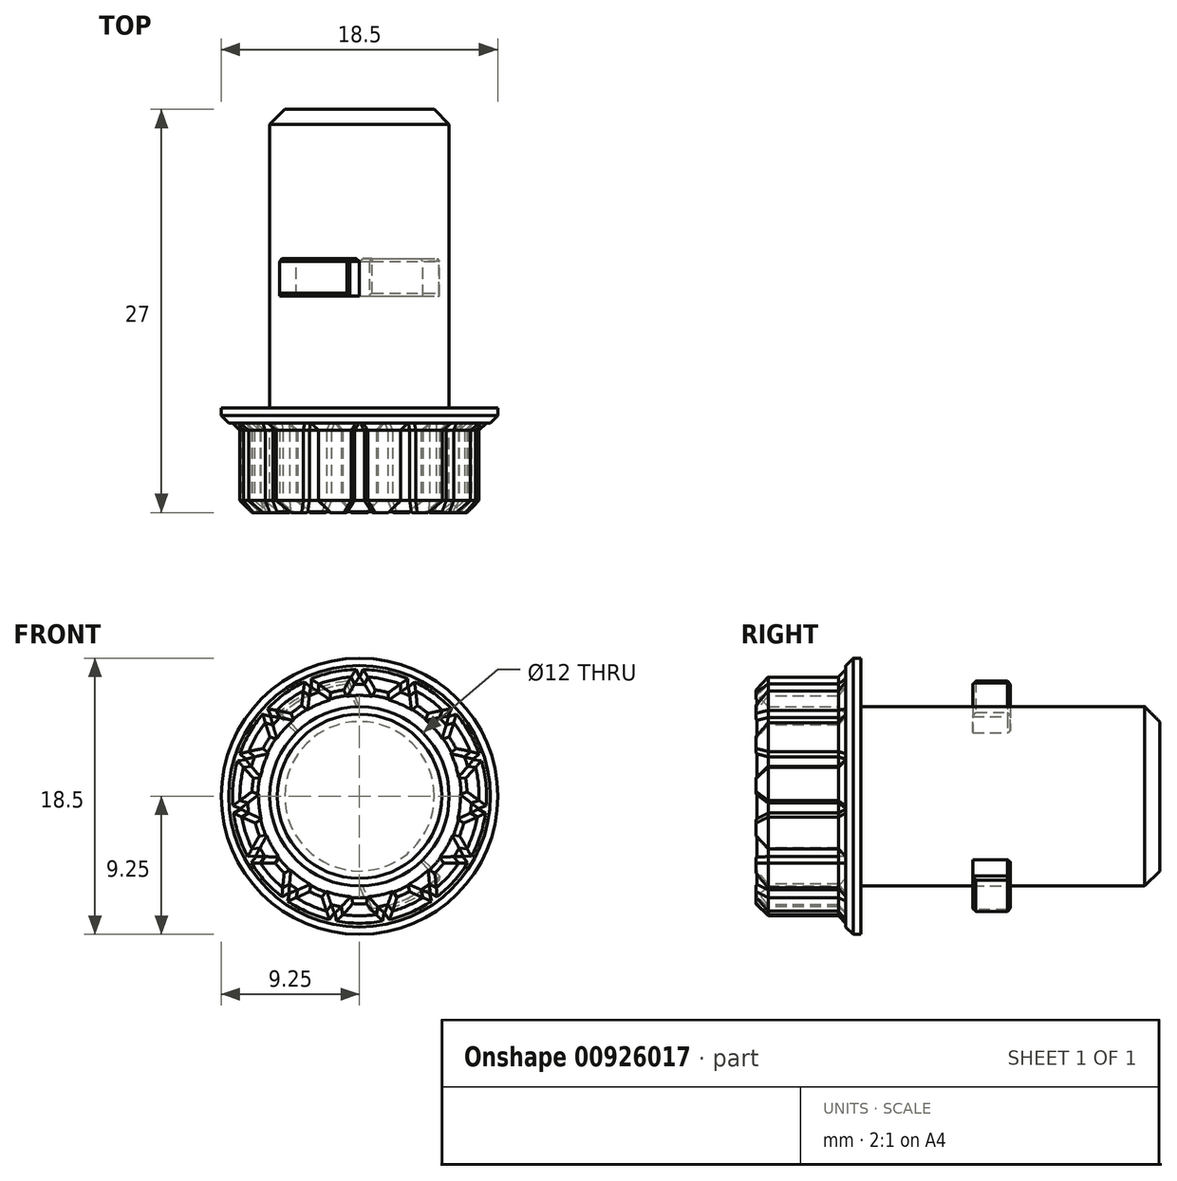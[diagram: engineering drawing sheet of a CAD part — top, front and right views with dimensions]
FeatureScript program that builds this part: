
annotation { "Feature Type Name" : "Feature", "Feature Type Description" : "" }
export const myFeature = defineFeature(function(context is Context, id is Id, definition is map)
    precondition{}
    {
        {
            var Q0;
            Q0=qCreatedBy(makeId("Front.planeOp"),FACE);
            var sketch = newSketch(context, id + "F0", { "sketchPlane" : qUnion([Q0])});
            skCircle(sketch, "E0", {"center": v(0, 0) * mm, "radius": 6 * mm});
            skArc(sketch, "E1", {"start": v(0.7, -7.72) * mm, "mid": v(3.29, -7.02) * mm, "end": v(5.48, -5.48) * mm});
            skLineSegment(sketch, "E2", {"start": v(-4.24, 4.24) * mm, "end": v(-5.48, 5.48) * mm});
            skLineSegment(sketch, "E3", {"start": v(4.24, -4.24) * mm, "end": v(5.48, -5.48) * mm});
            skArc(sketch, "E4.trimOffspring", {"start": v(-0.7, 7.72) * mm, "mid": v(-3.29, 7.02) * mm, "end": v(-5.48, 5.48) * mm});
            skLineSegment(sketch, "E5", {"start": v(0, 6) * mm, "end": v(-0.7, 7.72) * mm});
            skLineSegment(sketch, "E6", {"start": v(0, -6) * mm, "end": v(0.7, -7.72) * mm});
            skPoint(sketch, "E7.orphan", {"position": v(0, 7.75) * mm});
            skSolve(sketch);
        }
        {
            var Q0;
            Q0=qSketchRegion(id+"F0",true);
            extrude(context, id + "F1", {"entities" : qUnion([Q0]), "depth" : 10 * mm, "offsetDistance" : 25 * mm});
        }
        {
            var Q0;
            Q0=makeQuery(id+"F1.opExtrude","CAP_FACE",FACE,{"disambiguationData":[OSD([sQuery(id+"F0.wireOp",EDGE,"E0"),sQuery(id+"F0.wireOp",EDGE,"E1"),sQuery(id+"F0.wireOp",EDGE,"E2"),sQuery(id+"F0.wireOp",EDGE,"E3"),sQuery(id+"F0.wireOp",EDGE,"E4.trimOffspring"),sQuery(id+"F0.wireOp",EDGE,"E5"),sQuery(id+"F0.wireOp",EDGE,"E6")])],"isStart":false});
            var sketch = newSketch(context, id + "F2", { "sketchPlane" : qUnion([Q0])});
            skCircle(sketch, "E8", {"center": v(0, 0) * mm, "radius": 6 * mm});
            skSolve(sketch);
        }
        {
            var Q0;
            {var subQ1=makeQuery(id+"F1.opExtrude","CAP_EDGE",EDGE,{"disambiguationData":[OSD([sQuery(id+"F0.wireOp",EDGE,"E2")])],"isStart":false});Q0=makeQuery(id+"F2.imprint","IMPRINT",FACE,{"disambiguationData":[TD([[makeQuery(id+"F2.imprint","IMPRINT",EDGE,{"derivedFrom":subQ1}),-1.0]])]});}
            var Q1;
            Q1=makeQuery(id+"F2.imprint","IMPRINT",FACE,{"disambiguationData":[TD([[makeQuery(id+"F2.imprint","IMPRINT",EDGE,{"derivedFrom":makeQuery(id+"F1.opExtrude","CAP_EDGE",EDGE,{"disambiguationData":[OSD([sQuery(id+"F0.wireOp",EDGE,"E1")])],"isStart":false})}),1.0]])]});
            extrude(context, id + "F3", {"entities" : qUnion([Q0, Q1]), "operationType" : NewBodyOperationType.REMOVE, "oppositeDirection" : true, "depth" : 7.5 * mm, "offsetDistance" : 25 * mm});
        }
        {
            var Q0;
            Q0=makeQuery(id+"F1.opExtrude","CAP_FACE",FACE,{"disambiguationData":[OSD([sQuery(id+"F0.wireOp",EDGE,"E0"),sQuery(id+"F0.wireOp",EDGE,"E1"),sQuery(id+"F0.wireOp",EDGE,"E2"),sQuery(id+"F0.wireOp",EDGE,"E3"),sQuery(id+"F0.wireOp",EDGE,"E4.trimOffspring"),sQuery(id+"F0.wireOp",EDGE,"E5"),sQuery(id+"F0.wireOp",EDGE,"E6")])],"isStart":false});
            var sketch = newSketch(context, id + "F4", { "sketchPlane" : qUnion([Q0])});
            skCircle(sketch, "E9", {"center": v(0, 0) * mm, "radius": 8 * mm});
            skSolve(sketch);
        }
        {
            var Q0;
            Q0=makeQuery(id+"F4.imprint","IMPRINT",FACE,{"disambiguationData":[TD([[makeQuery(id+"F4.imprint","IMPRINT",EDGE,{"derivedFrom":sQuery(id+"F4.wireOp",EDGE,"E9")}),1.0]])]});
            var Q1;
            {var subQ0=sQuery(id+"F2.wireOp",EDGE,"E8");var subQ1=sQuery(id+"F0.wireOp",EDGE,"E3");var subQ3=sQuery(id+"F0.wireOp",EDGE,"E2");var subQ5=sQuery(id+"F0.wireOp",EDGE,"E0");Q1=makeQuery(id+"F4.imprint","IMPRINT",FACE,{"disambiguationData":[TD([[makeQuery(id+"F4.imprint","IMPRINT",EDGE,{"derivedFrom":makeQuery(id+"F3.boolean.opBoolean","MERGE",EDGE,{"derivedFrom":[makeQuery(id+"F1.opExtrude","CAP_EDGE",EDGE,{"disambiguationData":[OSD([subQ5]),TDD([makeQuery(id+"F0.imprint","IMPRINT",EDGE,{"disambiguationData":[TD([[makeQuery(id+"F0.imprint","INTERSECT",VERTEX,{"derivedFrom":[subQ5,subQ3]}),-1.0]])],"derivedFrom":subQ5})])],"isStart":false}),makeQuery(id+"F1.opExtrude","CAP_EDGE",EDGE,{"disambiguationData":[OSD([subQ5]),TDD([makeQuery(id+"F0.imprint","IMPRINT",EDGE,{"disambiguationData":[TD([[makeQuery(id+"F0.imprint","INTERSECT",VERTEX,{"derivedFrom":[subQ5,subQ1]}),-1.0]])],"derivedFrom":subQ5})])],"isStart":false})],"fromTools":[makeQuery(id+"F3.opExtrude","CAP_EDGE",EDGE,{"disambiguationData":[OSD([subQ0]),TDD([makeQuery(id+"F2.imprint","IMPRINT",EDGE,{"disambiguationData":[TD([[makeQuery(id+"F2.imprint","INTERSECT",VERTEX,{"derivedFrom":[makeQuery(id+"F1.opExtrude","CAP_EDGE",EDGE,{"disambiguationData":[OSD([subQ3])],"isStart":false}),subQ0]}),1.0]])],"derivedFrom":subQ0})])],"isStart":true}),makeQuery(id+"F3.opExtrude","CAP_EDGE",EDGE,{"disambiguationData":[OSD([subQ0]),TDD([makeQuery(id+"F2.imprint","IMPRINT",EDGE,{"disambiguationData":[TD([[makeQuery(id+"F2.imprint","INTERSECT",VERTEX,{"derivedFrom":[makeQuery(id+"F1.opExtrude","CAP_EDGE",EDGE,{"disambiguationData":[OSD([subQ1])],"isStart":false}),subQ0]}),1.0]])],"derivedFrom":subQ0})])],"isStart":true})]})}),1.0]])]});}
            extrude(context, id + "F5", {"entities" : qUnion([Q0, Q1]), "operationType" : NewBodyOperationType.ADD, "depth" : 7 * mm, "offsetDistance" : 25 * mm});
        }
        {
            var Q0;
            Q0=makeQuery(id+"F1.opExtrude","CAP_FACE",FACE,{"disambiguationData":[OSD([sQuery(id+"F0.wireOp",EDGE,"E0"),sQuery(id+"F0.wireOp",EDGE,"E1"),sQuery(id+"F0.wireOp",EDGE,"E2"),sQuery(id+"F0.wireOp",EDGE,"E3"),sQuery(id+"F0.wireOp",EDGE,"E4.trimOffspring"),sQuery(id+"F0.wireOp",EDGE,"E5"),sQuery(id+"F0.wireOp",EDGE,"E6")])],"isStart":true});
            var sketch = newSketch(context, id + "F6", { "sketchPlane" : qUnion([Q0])});
            skCircle(sketch, "E10", {"center": v(0, 0) * mm, "radius": 6 * mm});
            skSolve(sketch);
        }
        {
            var Q0;
            Q0=qSketchRegion(id+"F6",true);
            extrude(context, id + "F7", {"entities" : qUnion([Q0]), "operationType" : NewBodyOperationType.ADD, "depth" : 10 * mm, "offsetDistance" : 25 * mm});
        }
        {
            var Q0;
            Q0=makeQuery(id+"F5.opExtrude","CAP_FACE",FACE,{"disambiguationData":[OSD([sQuery(id+"F4.wireOp",EDGE,"E9")])],"isStart":false});
            var sketch = newSketch(context, id + "F8", { "sketchPlane" : qUnion([Q0])});
            skCircle(sketch, "E11", {"center": v(0, 0) * mm, "radius": 7.5 * mm});
            skLineSegment(sketch, "E12", {"start": v(-0.56, 7.98) * mm, "end": v(-0.34, 7.5) * mm});
            skLineSegment(sketch, "E13", {"start": v(0.56, 7.98) * mm, "end": v(0.34, 7.5) * mm});
            skLineSegment(sketch, "E14.1.0", {"start": v(-2.74, 7.52) * mm, "end": v(-2.74, 6.98) * mm});
            skLineSegment(sketch, "E14.1.1", {"start": v(-3.76, 7.06) * mm, "end": v(-3.36, 6.7) * mm});
            skLineSegment(sketch, "E14.2.0", {"start": v(-5.56, 5.75) * mm, "end": v(-5.34, 5.27) * mm});
            skLineSegment(sketch, "E14.2.1", {"start": v(-6.3, 4.93) * mm, "end": v(-5.8, 4.76) * mm});
            skLineSegment(sketch, "E14.3.0", {"start": v(-7.42, 3) * mm, "end": v(-7.02, 2.64) * mm});
            skLineSegment(sketch, "E14.3.1", {"start": v(-7.76, 1.94) * mm, "end": v(-7.23, 2) * mm});
            skLineSegment(sketch, "E14.4.0", {"start": v(-8, -0.28) * mm, "end": v(-7.49, -0.44) * mm});
            skLineSegment(sketch, "E14.4.1", {"start": v(-7.88, -1.39) * mm, "end": v(-7.42, -1.12) * mm});
            skLineSegment(sketch, "E14.5.0", {"start": v(-7.2, -3.5) * mm, "end": v(-6.66, -3.45) * mm});
            skLineSegment(sketch, "E14.5.1", {"start": v(-6.63, -4.47) * mm, "end": v(-6.32, -4.04) * mm});
            skLineSegment(sketch, "E14.6.0", {"start": v(-5.14, -6.13) * mm, "end": v(-4.68, -5.86) * mm});
            skLineSegment(sketch, "E14.6.1", {"start": v(-4.24, -6.78) * mm, "end": v(-4.13, -6.26) * mm});
            skLineSegment(sketch, "E14.7.0", {"start": v(-2.2, -7.7) * mm, "end": v(-1.9, -7.26) * mm});
            skLineSegment(sketch, "E14.7.1", {"start": v(-1.11, -7.92) * mm, "end": v(-1.22, -7.4) * mm});
            skLineSegment(sketch, "E14.8.0", {"start": v(1.11, -7.92) * mm, "end": v(1.22, -7.4) * mm});
            skLineSegment(sketch, "E14.8.1", {"start": v(2.2, -7.7) * mm, "end": v(1.9, -7.26) * mm});
            skLineSegment(sketch, "E14.9.0", {"start": v(4.24, -6.78) * mm, "end": v(4.13, -6.26) * mm});
            skLineSegment(sketch, "E14.9.1", {"start": v(5.14, -6.13) * mm, "end": v(4.68, -5.86) * mm});
            skLineSegment(sketch, "E14.10.0", {"start": v(6.63, -4.47) * mm, "end": v(6.32, -4.04) * mm});
            skLineSegment(sketch, "E14.10.1", {"start": v(7.2, -3.5) * mm, "end": v(6.66, -3.45) * mm});
            skLineSegment(sketch, "E14.11.0", {"start": v(7.88, -1.39) * mm, "end": v(7.42, -1.12) * mm});
            skLineSegment(sketch, "E14.11.1", {"start": v(8, -0.28) * mm, "end": v(7.49, -0.44) * mm});
            skLineSegment(sketch, "E14.12.0", {"start": v(7.76, 1.94) * mm, "end": v(7.23, 2) * mm});
            skLineSegment(sketch, "E14.12.1", {"start": v(7.42, 3) * mm, "end": v(7.02, 2.64) * mm});
            skLineSegment(sketch, "E14.13.0", {"start": v(6.3, 4.93) * mm, "end": v(5.8, 4.76) * mm});
            skLineSegment(sketch, "E14.13.1", {"start": v(5.56, 5.75) * mm, "end": v(5.34, 5.27) * mm});
            skLineSegment(sketch, "E14.14.0", {"start": v(3.76, 7.06) * mm, "end": v(3.36, 6.7) * mm});
            skLineSegment(sketch, "E14.14.1", {"start": v(2.74, 7.52) * mm, "end": v(2.74, 6.98) * mm});
            skSolve(sketch);
        }
        {
            var Q0;
            {var subQ0=sQuery(id+"F8.wireOp",EDGE,"E12");Q0=makeQuery(id+"F8.imprint","IMPRINT",FACE,{"disambiguationData":[TD([[makeQuery(id+"F8.imprint","IMPRINT",EDGE,{"derivedFrom":subQ0}),1.0]])]});}
            var Q1;
            {var subQ0=sQuery(id+"F8.wireOp",EDGE,"E14.24.0");Q1=makeQuery(id+"F8.imprint","IMPRINT",FACE,{"disambiguationData":[TD([[makeQuery(id+"F8.imprint","IMPRINT",EDGE,{"derivedFrom":subQ0}),-1.0]])]});}
            var Q2;
            {var subQ0=sQuery(id+"F8.wireOp",EDGE,"E14.23.0");Q2=makeQuery(id+"F8.imprint","IMPRINT",FACE,{"disambiguationData":[TD([[makeQuery(id+"F8.imprint","IMPRINT",EDGE,{"derivedFrom":subQ0}),-1.0]])]});}
            var Q3;
            {var subQ0=sQuery(id+"F8.wireOp",EDGE,"E14.22.0");Q3=makeQuery(id+"F8.imprint","IMPRINT",FACE,{"disambiguationData":[TD([[makeQuery(id+"F8.imprint","IMPRINT",EDGE,{"derivedFrom":subQ0}),-1.0]])]});}
            var Q4;
            {var subQ0=sQuery(id+"F8.wireOp",EDGE,"E14.21.0");Q4=makeQuery(id+"F8.imprint","IMPRINT",FACE,{"disambiguationData":[TD([[makeQuery(id+"F8.imprint","IMPRINT",EDGE,{"derivedFrom":subQ0}),-1.0]])]});}
            var Q5;
            {var subQ0=sQuery(id+"F8.wireOp",EDGE,"E14.20.0");Q5=makeQuery(id+"F8.imprint","IMPRINT",FACE,{"disambiguationData":[TD([[makeQuery(id+"F8.imprint","IMPRINT",EDGE,{"derivedFrom":subQ0}),-1.0]])]});}
            var Q6;
            {var subQ0=sQuery(id+"F8.wireOp",EDGE,"E14.19.0");Q6=makeQuery(id+"F8.imprint","IMPRINT",FACE,{"disambiguationData":[TD([[makeQuery(id+"F8.imprint","IMPRINT",EDGE,{"derivedFrom":subQ0}),-1.0]])]});}
            var Q7;
            {var subQ0=sQuery(id+"F8.wireOp",EDGE,"E14.17.0");Q7=makeQuery(id+"F8.imprint","IMPRINT",FACE,{"disambiguationData":[TD([[makeQuery(id+"F8.imprint","IMPRINT",EDGE,{"derivedFrom":subQ0}),-1.0]])]});}
            var Q8;
            {var subQ0=sQuery(id+"F8.wireOp",EDGE,"E14.16.0");Q8=makeQuery(id+"F8.imprint","IMPRINT",FACE,{"disambiguationData":[TD([[makeQuery(id+"F8.imprint","IMPRINT",EDGE,{"derivedFrom":subQ0}),-1.0]])]});}
            var Q9;
            {var subQ0=sQuery(id+"F8.wireOp",EDGE,"E14.15.0");Q9=makeQuery(id+"F8.imprint","IMPRINT",FACE,{"disambiguationData":[TD([[makeQuery(id+"F8.imprint","IMPRINT",EDGE,{"derivedFrom":subQ0}),-1.0]])]});}
            var Q10;
            {var subQ0=sQuery(id+"F8.wireOp",EDGE,"E14.14.0");Q10=makeQuery(id+"F8.imprint","IMPRINT",FACE,{"disambiguationData":[TD([[makeQuery(id+"F8.imprint","IMPRINT",EDGE,{"derivedFrom":subQ0}),-1.0]])]});}
            var Q11;
            {var subQ0=sQuery(id+"F8.wireOp",EDGE,"E14.13.0");Q11=makeQuery(id+"F8.imprint","IMPRINT",FACE,{"disambiguationData":[TD([[makeQuery(id+"F8.imprint","IMPRINT",EDGE,{"derivedFrom":subQ0}),-1.0]])]});}
            var Q12;
            {var subQ0=sQuery(id+"F8.wireOp",EDGE,"E14.12.0");Q12=makeQuery(id+"F8.imprint","IMPRINT",FACE,{"disambiguationData":[TD([[makeQuery(id+"F8.imprint","IMPRINT",EDGE,{"derivedFrom":subQ0}),-1.0]])]});}
            var Q13;
            {var subQ0=sQuery(id+"F8.wireOp",EDGE,"E14.11.0");Q13=makeQuery(id+"F8.imprint","IMPRINT",FACE,{"disambiguationData":[TD([[makeQuery(id+"F8.imprint","IMPRINT",EDGE,{"derivedFrom":subQ0}),-1.0]])]});}
            var Q14;
            {var subQ0=sQuery(id+"F8.wireOp",EDGE,"E14.10.0");Q14=makeQuery(id+"F8.imprint","IMPRINT",FACE,{"disambiguationData":[TD([[makeQuery(id+"F8.imprint","IMPRINT",EDGE,{"derivedFrom":subQ0}),-1.0]])]});}
            var Q15;
            {var subQ0=sQuery(id+"F8.wireOp",EDGE,"E14.9.0");Q15=makeQuery(id+"F8.imprint","IMPRINT",FACE,{"disambiguationData":[TD([[makeQuery(id+"F8.imprint","IMPRINT",EDGE,{"derivedFrom":subQ0}),-1.0]])]});}
            var Q16;
            {var subQ0=sQuery(id+"F8.wireOp",EDGE,"E14.8.0");Q16=makeQuery(id+"F8.imprint","IMPRINT",FACE,{"disambiguationData":[TD([[makeQuery(id+"F8.imprint","IMPRINT",EDGE,{"derivedFrom":subQ0}),-1.0]])]});}
            var Q17;
            {var subQ0=sQuery(id+"F8.wireOp",EDGE,"E14.7.0");Q17=makeQuery(id+"F8.imprint","IMPRINT",FACE,{"disambiguationData":[TD([[makeQuery(id+"F8.imprint","IMPRINT",EDGE,{"derivedFrom":subQ0}),-1.0]])]});}
            var Q18;
            {var subQ0=sQuery(id+"F8.wireOp",EDGE,"E14.6.0");Q18=makeQuery(id+"F8.imprint","IMPRINT",FACE,{"disambiguationData":[TD([[makeQuery(id+"F8.imprint","IMPRINT",EDGE,{"derivedFrom":subQ0}),-1.0]])]});}
            var Q19;
            {var subQ0=sQuery(id+"F8.wireOp",EDGE,"E14.5.0");Q19=makeQuery(id+"F8.imprint","IMPRINT",FACE,{"disambiguationData":[TD([[makeQuery(id+"F8.imprint","IMPRINT",EDGE,{"derivedFrom":subQ0}),-1.0]])]});}
            var Q20;
            {var subQ0=sQuery(id+"F8.wireOp",EDGE,"E14.4.0");Q20=makeQuery(id+"F8.imprint","IMPRINT",FACE,{"disambiguationData":[TD([[makeQuery(id+"F8.imprint","IMPRINT",EDGE,{"derivedFrom":subQ0}),-1.0]])]});}
            var Q21;
            {var subQ0=sQuery(id+"F8.wireOp",EDGE,"E14.3.0");Q21=makeQuery(id+"F8.imprint","IMPRINT",FACE,{"disambiguationData":[TD([[makeQuery(id+"F8.imprint","IMPRINT",EDGE,{"derivedFrom":subQ0}),-1.0]])]});}
            var Q22;
            {var subQ0=sQuery(id+"F8.wireOp",EDGE,"E14.2.0");Q22=makeQuery(id+"F8.imprint","IMPRINT",FACE,{"disambiguationData":[TD([[makeQuery(id+"F8.imprint","IMPRINT",EDGE,{"derivedFrom":subQ0}),-1.0]])]});}
            var Q23;
            {var subQ0=sQuery(id+"F8.wireOp",EDGE,"E14.1.0");Q23=makeQuery(id+"F8.imprint","IMPRINT",FACE,{"disambiguationData":[TD([[makeQuery(id+"F8.imprint","IMPRINT",EDGE,{"derivedFrom":subQ0}),-1.0]])]});}
            var Q24;
            {var subQ0=sQuery(id+"F8.wireOp",EDGE,"E14.18.0");Q24=makeQuery(id+"F8.imprint","IMPRINT",FACE,{"disambiguationData":[TD([[makeQuery(id+"F8.imprint","IMPRINT",EDGE,{"derivedFrom":subQ0}),-1.0]])]});}
            extrude(context, id + "F9", {"entities" : qUnion([Q0, Q1, Q2, Q3, Q4, Q5, Q6, Q7, Q8, Q9, Q10, Q11, Q12, Q13, Q14, Q15, Q16, Q17, Q18, Q19, Q20, Q21, Q22, Q23, Q24]), "operationType" : NewBodyOperationType.REMOVE, "oppositeDirection" : true, "depth" : 10 * mm, "offsetDistance" : 25 * mm});
        }
        {
            var Q0;
            Q0=makeQuery(id+"F5.opExtrude","CAP_FACE",FACE,{"disambiguationData":[OSD([sQuery(id+"F4.wireOp",EDGE,"E9")])],"isStart":true});
            var sketch = newSketch(context, id + "F10", { "sketchPlane" : qUnion([Q0])});
            skCircle(sketch, "E15", {"center": v(0, 0) * mm, "radius": 9.25 * mm});
            skSolve(sketch);
        }
        {
            var Q0;
            Q0 = qSketchRegion(id + "F10", true);
            extrude(context, id + "F11", {"entities" : qUnion([Q0]), "operationType" : NewBodyOperationType.ADD, "oppositeDirection" : true, "depth" : 1 * mm, "offsetDistance" : 25 * mm});
        }
        {
            var Q0;
            Q0=makeQuery(id+"F11.opExtrude","CAP_FACE",FACE,{"disambiguationData":[OSD([sQuery(id+"F10.wireOp",EDGE,"E15")])],"isStart":false});
            chamfer(context, id + "F12", {"entities" : qUnion([Q0]), "width" : 0.5 * mm, "tangentPropagation" : true});
        }
        {
            var Q0;
            Q0=makeQuery(id+"F5.opExtrude","CAP_FACE",FACE,{"disambiguationData":[OSD([sQuery(id+"F4.wireOp",EDGE,"E9")])],"isStart":false});
            chamfer(context, id + "F13", {"entities" : qUnion([Q0]), "width" : 0.8 * mm, "tangentPropagation" : true});
        }
        {
            var Q0;
            Q0=makeQuery(id+"F7.opExtrude","CAP_EDGE",EDGE,{"disambiguationData":[OSD([sQuery(id+"F6.wireOp",EDGE,"E10")])],"isStart":false});
            chamfer(context, id + "F14", {"entities" : qUnion([Q0]), "width" : 1 * mm, "tangentPropagation" : true});
        }
        {
            var Q0;
            Q0=makeQuery(id+"F3.boolean.opBoolean","COPY",EDGE,{"derivedFrom":makeQuery(id+"F3.opExtrude","CAP_EDGE",EDGE,{"disambiguationData":[OSD([sQuery(id+"F0.wireOp",EDGE,"E5")])],"isStart":false})});
            var Q1;
            Q1=makeQuery(id+"F1.opExtrude","SWEPT_EDGE",EDGE,{"disambiguationData":[OSD([sQuery(id+"F0.wireOp",EDGE,"E4.trimOffspring"),sQuery(id+"F0.wireOp",EDGE,"E5")])]});
            var Q2;
            Q2=makeQuery(id+"F1.opExtrude","CAP_EDGE",EDGE,{"disambiguationData":[OSD([sQuery(id+"F0.wireOp",EDGE,"E5")])],"isStart":true});
            var Q3;
            Q3=makeQuery(id+"F1.opExtrude","CAP_EDGE",EDGE,{"disambiguationData":[OSD([sQuery(id+"F0.wireOp",EDGE,"E4.trimOffspring")])],"isStart":true});
            var Q4;
            Q4=makeQuery(id+"F3.boolean.opBoolean","COPY",EDGE,{"derivedFrom":makeQuery(id+"F3.opExtrude","CAP_EDGE",EDGE,{"disambiguationData":[OSD([sQuery(id+"F0.wireOp",EDGE,"E4.trimOffspring")])],"isStart":false})});
            var Q5;
            Q5=makeQuery(id+"F1.opExtrude","SWEPT_FACE",FACE,{"disambiguationData":[OSD([sQuery(id+"F0.wireOp",EDGE,"E4.trimOffspring")])]});
            var Q6;
            Q6=makeQuery(id+"F1.opExtrude","CAP_EDGE",EDGE,{"disambiguationData":[OSD([sQuery(id+"F0.wireOp",EDGE,"E2")])],"isStart":true});
            var Q7;
            Q7=makeQuery(id+"F3.boolean.opBoolean","COPY",EDGE,{"derivedFrom":makeQuery(id+"F3.opExtrude","CAP_EDGE",EDGE,{"disambiguationData":[OSD([sQuery(id+"F0.wireOp",EDGE,"E2")])],"isStart":false})});
            var Q8;
            Q8=makeQuery(id+"F1.opExtrude","SWEPT_FACE",FACE,{"disambiguationData":[OSD([sQuery(id+"F0.wireOp",EDGE,"E1")])]});
            var Q9;
            Q9=makeQuery(id+"F1.opExtrude","CAP_EDGE",EDGE,{"disambiguationData":[OSD([sQuery(id+"F0.wireOp",EDGE,"E6")])],"isStart":true});
            var Q10;
            Q10=makeQuery(id+"F3.boolean.opBoolean","COPY",EDGE,{"derivedFrom":makeQuery(id+"F3.opExtrude","CAP_EDGE",EDGE,{"disambiguationData":[OSD([sQuery(id+"F0.wireOp",EDGE,"E6")])],"isStart":false})});
            var Q11;
            Q11=makeQuery(id+"F1.opExtrude","CAP_EDGE",EDGE,{"disambiguationData":[OSD([sQuery(id+"F0.wireOp",EDGE,"E3")])],"isStart":true});
            var Q12;
            Q12=makeQuery(id+"F3.boolean.opBoolean","COPY",EDGE,{"derivedFrom":makeQuery(id+"F3.opExtrude","CAP_EDGE",EDGE,{"disambiguationData":[OSD([sQuery(id+"F0.wireOp",EDGE,"E3")])],"isStart":false})});
            chamfer(context, id + "F15", {"entities" : qUnion([Q0, Q1, Q2, Q3, Q4, Q5, Q6, Q7, Q8, Q9, Q10, Q11, Q12]), "width" : 0.2 * mm, "tangentPropagation" : true});
        }
    });
